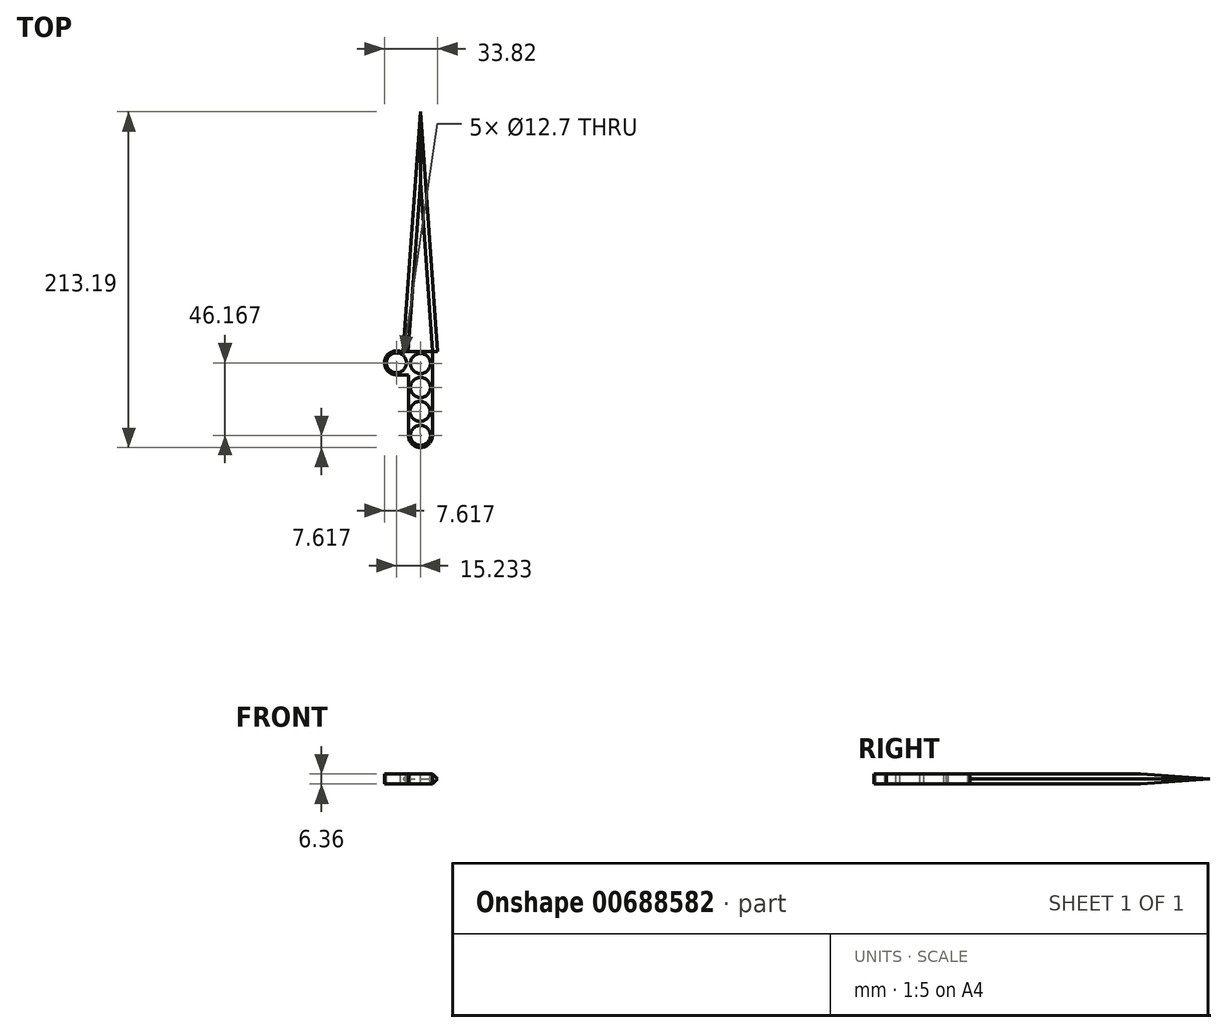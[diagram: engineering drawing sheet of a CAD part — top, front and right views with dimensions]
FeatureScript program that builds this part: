
annotation { "Feature Type Name" : "Feature", "Feature Type Description" : "" }
export const myFeature = defineFeature(function(context is Context, id is Id, definition is map)
    precondition{}
    {
        {
            var Q0;
            Q0=qCreatedBy(makeId("Top.planeOp"),FACE);
            var sketch = newSketch(context, id + "F0", { "sketchPlane" : qUnion([Q0])});
            skLineSegment(sketch, "E0", {"start": v(-10.97, -50.64) * mm, "end": v(10.97, -50.64) * mm});
            skLineSegment(sketch, "E1", {"start": v(0, 101.6) * mm, "end": v(-10.97, -50.64) * mm});
            skLineSegment(sketch, "E2", {"start": v(10.97, -50.64) * mm, "end": v(0, 101.6) * mm});
            skSolve(sketch);
        }
        {
            var Q0;
            Q0=makeQuery(id+"F0.imprint","IMPRINT",FACE,{"disambiguationData":[TD([[makeQuery(id+"F0.imprint","IMPRINT",EDGE,{"derivedFrom":sQuery(id+"F0.wireOp",EDGE,"x6LDntK3-yeNv-eLWQ-GN5G-AI2rOA0EEMsQ")}),1.0]])]});
            var Q1;
            Q1=makeQuery(id+"F0.imprint","IMPRINT",FACE,{"disambiguationData":[TD([[makeQuery(id+"F0.imprint","IMPRINT",EDGE,{"derivedFrom":sQuery(id+"F0.wireOp",EDGE,"E0")}),1.0]])]});
            var Q2;
            Q2=sQuery(id+"F0.wireOp",EDGE,"x6LDntK3-yeNv-eLWQ-GN5G-AI2rOA0EEMsQ");
            var Q3;
            Q3=sQuery(id+"F0.wireOp",EDGE,"E0");
            extrude(context, id + "F1", {"entities" : qUnion([Q0, Q1]), "surfaceEntities" : qUnion([Q2, Q3]), "endBound" : BoundingType.SYMMETRIC, "depth" : 6.35 * mm, "offsetDistance" : 25.4 * mm});
        }
        {
            var Q0;
            Q0=makeQuery(id+"F1.opExtrude","CAP_EDGE",EDGE,{"disambiguationData":[OSD([sQuery(id+"F0.wireOp",EDGE,"E2")])],"isStart":false});
            var Q1;
            Q1=makeQuery(id+"F1.opExtrude","CAP_EDGE",EDGE,{"disambiguationData":[OSD([sQuery(id+"F0.wireOp",EDGE,"E1")])],"isStart":false});
            var Q2;
            Q2=makeQuery(id+"F1.opExtrude","CAP_EDGE",EDGE,{"disambiguationData":[OSD([sQuery(id+"F0.wireOp",EDGE,"E2")])],"isStart":true});
            var Q3;
            Q3=makeQuery(id+"F1.opExtrude","CAP_EDGE",EDGE,{"disambiguationData":[OSD([sQuery(id+"F0.wireOp",EDGE,"E1")])],"isStart":true});
            chamfer(context, id + "F2", {"entities" : qUnion([Q0, Q1, Q2, Q3]), "width" : 3.17 * mm, "tangentPropagation" : true});
        }
        {
            var Q0;
            Q0=makeQuery(id+"F1.opExtrude","CAP_FACE",FACE,{"disambiguationData":[OSD([sQuery(id+"F0.wireOp",EDGE,"E0"),sQuery(id+"F0.wireOp",EDGE,"E1"),sQuery(id+"F0.wireOp",EDGE,"E2")])],"isStart":false});
            var sketch = newSketch(context, id + "F3", { "sketchPlane" : qUnion([Q0])});
            skArc(sketch, "E3", {"start": v(-7.62, -58.03) * mm, "mid": v(-7.62, -58.15) * mm, "end": v(-7.62, -58.26) * mm});
            skArc(sketch, "E4", {"start": v(-7.6, -104.55) * mm, "mid": v(0.36, -111.58) * mm, "end": v(7.62, -103.82) * mm});
            skArc(sketch, "E5", {"start": v(-12.65, -50.64) * mm, "mid": v(-22.72, -56.38) * mm, "end": v(-15.46, -65.42) * mm});
            skCircle(sketch, "E6", {"center": v(0, -58.26) * mm, "radius": 6.35 * mm});
            skCircle(sketch, "E7", {"center": v(0, -73.5) * mm, "radius": 6.35 * mm});
            skCircle(sketch, "E8", {"center": v(-0.28, -88.74) * mm, "radius": 6.35 * mm});
            skCircle(sketch, "E9", {"center": v(0, -103.97) * mm, "radius": 6.35 * mm});
            skCircle(sketch, "E10", {"center": v(-15.23, -57.8) * mm, "radius": 6.35 * mm});
            skLineSegment(sketch, "E11", {"start": v(7.62, -103.82) * mm, "end": v(7.8, -50.64) * mm});
            skLineSegment(sketch, "E12", {"start": v(-7.6, -104.55) * mm, "end": v(-7.62, -65.65) * mm});
            skLineSegment(sketch, "E13", {"start": v(0, -50.64) * mm, "end": v(-12.65, -50.64) * mm});
            skLineSegment(sketch, "E14.trimOffspring", {"start": v(-7.62, -58.26) * mm, "end": v(-7.62, -58.13) * mm});
            skArc(sketch, "E15.trimOffspring", {"start": v(-7.62, -58.13) * mm, "mid": v(-7.62, -58.08) * mm, "end": v(-7.62, -58.03) * mm});
            skLineSegment(sketch, "E16.trimOffspring", {"start": v(-7.62, -65.65) * mm, "end": v(-15.46, -65.42) * mm});
            skPoint(sketch, "E17.start.orphan", {"position": v(0, -65.88) * mm});
            skSolve(sketch);
        }
        {
            var Q0;
            Q0=makeQuery(id+"F3.imprint","IMPRINT",FACE,{"disambiguationData":[TD([[makeQuery(id+"F3.imprint","IMPRINT",EDGE,{"derivedFrom":sQuery(id+"F3.wireOp",EDGE,"E3")}),-1.0]])]});
            var Q1;
            Q1=makeQuery(id+"F3.imprint","IMPRINT",FACE,{"disambiguationData":[TD([[makeQuery(id+"F3.imprint","IMPRINT",EDGE,{"derivedFrom":sQuery(id+"F3.wireOp",EDGE,"E3")}),1.0]])]});
            extrude(context, id + "F4", {"entities" : qUnion([Q0, Q1]), "oppositeDirection" : true, "depth" : 6.35 * mm, "offsetDistance" : 25.4 * mm});
        }
    });
